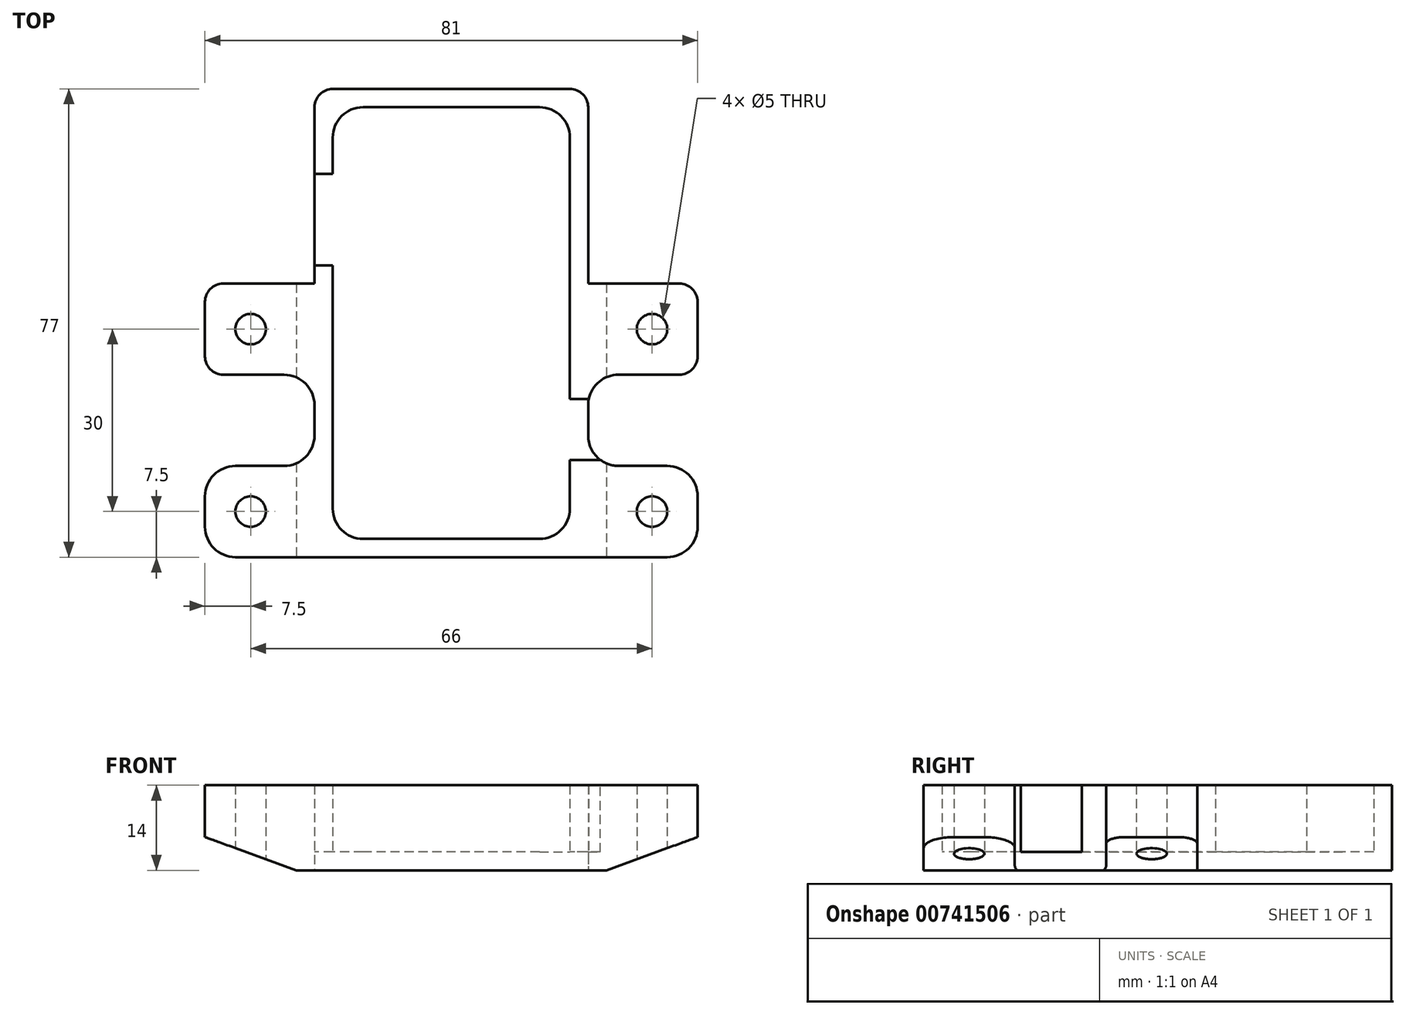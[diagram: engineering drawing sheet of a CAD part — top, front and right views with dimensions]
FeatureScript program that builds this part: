
annotation { "Feature Type Name" : "Feature", "Feature Type Description" : "" }
export const myFeature = defineFeature(function(context is Context, id is Id, definition is map)
    precondition{}
    {
        {
            var Q0;
            Q0=qCreatedBy(makeId("Top.planeOp"),FACE);
            var sketch = newSketch(context, id + "F0", { "sketchPlane" : qUnion([Q0])});
            skLineSegment(sketch, "E0.bottom", {"start": v(22.5, 38.5) * mm, "end": v(-22.5, 38.5) * mm});
            skLineSegment(sketch, "E0.top", {"start": v(22.5, -38.5) * mm, "end": v(-22.5, -38.5) * mm});
            skLineSegment(sketch, "E0.left", {"start": v(22.5, 38.5) * mm, "end": v(22.5, -38.5) * mm});
            skLineSegment(sketch, "E0.right", {"start": v(-22.5, 38.5) * mm, "end": v(-22.5, -38.5) * mm});
            skPoint(sketch, "E0.middle", {"position": v(0, 0) * mm});
            skSolve(sketch);
        }
        {
            var Q0;
            Q0 = qSketchRegion(id + "F0", true);
            extrude(context, id + "F1", {"entities" : qUnion([Q0]), "depth" : 3 * mm, "offsetDistance" : 25 * mm});
        }
        {
            var Q0;
            Q0=makeQuery(id+"F1.opExtrude","CAP_FACE",FACE,{"disambiguationData":[OSD([sQuery(id+"F0.wireOp",EDGE,"E0.bottom"),sQuery(id+"F0.wireOp",EDGE,"E0.top"),sQuery(id+"F0.wireOp",EDGE,"E0.left"),sQuery(id+"F0.wireOp",EDGE,"E0.right")])],"isStart":false});
            var sketch = newSketch(context, id + "F2", { "sketchPlane" : qUnion([Q0])});
            skSolve(sketch);
        }
        {
            var Q0;
            Q0=makeQuery(id+"F2.imprint","IMPRINT",FACE,{"disambiguationData":[TD([[makeQuery(id+"F2.imprint","IMPRINT",EDGE,{"derivedFrom":makeQuery(id+"F1.opExtrude","CAP_EDGE",EDGE,{"disambiguationData":[OSD([sQuery(id+"F0.wireOp",EDGE,"E0.bottom")])],"isStart":false})}),1.0]])]});
            var sketch = newSketch(context, id + "F3", { "sketchPlane" : qUnion([Q0])});
            skLineSegment(sketch, "E1", {"start": v(25.25, -12.5) * mm, "end": v(19.5, -12.5) * mm});
            skLineSegment(sketch, "E2", {"start": v(19.5, -12.5) * mm, "end": v(19.5, 35.5) * mm});
            skLineSegment(sketch, "E3", {"start": v(19.5, 35.5) * mm, "end": v(-19.5, 35.5) * mm});
            skLineSegment(sketch, "E4", {"start": v(-19.5, 35.5) * mm, "end": v(-19.5, 24.5) * mm});
            skLineSegment(sketch, "E5", {"start": v(-19.5, 24.5) * mm, "end": v(-28, 24.5) * mm});
            skLineSegment(sketch, "E6", {"start": v(28, -22.5) * mm, "end": v(19.5, -22.5) * mm});
            skLineSegment(sketch, "E7", {"start": v(19.5, -22.5) * mm, "end": v(19.5, -22.75) * mm});
            skLineSegment(sketch, "E8", {"start": v(19.5, -22.75) * mm, "end": v(19.5, -35.5) * mm});
            skLineSegment(sketch, "E9", {"start": v(-28, 9.5) * mm, "end": v(-19.5, 9.5) * mm});
            skLineSegment(sketch, "E10", {"start": v(-19.5, 9.5) * mm, "end": v(-19.5, -35.5) * mm});
            skPoint(sketch, "E11", {"position": v(-26.46, -18.57) * mm});
            skPoint(sketch, "E12", {"position": v(23.75, -11.55) * mm});
            skPoint(sketch, "E12.positionSnap0", {"position": v(23.75, -22.5) * mm});
            skLineSegment(sketch, "E13", {"start": v(-19.5, -35.5) * mm, "end": v(19.5, -35.5) * mm});
            skSolve(sketch);
        }
        {
            var Q0;
            Q0=makeQuery(id+"F3.imprint","IMPRINT",FACE,{"disambiguationData":[TD([[makeQuery(id+"F3.imprint","IMPRINT",EDGE,{"derivedFrom":sQuery(id+"F3.wireOp",EDGE,"SLzFKG8K-n8H2-2ykC-QiUt-zYdIRSfNmcF6.bottom")}),-1.0]])]});
            var Q1;
            {var subQ2=sQuery(id+"F3.wireOp",EDGE,"E1");Q1=makeQuery(id+"F3.imprint","IMPRINT",FACE,{"disambiguationData":[TD([[makeQuery(id+"F3.imprint","IMPRINT",EDGE,{"derivedFrom":subQ2}),-1.0]])]});}
            var Q2;
            {var subQ3=sQuery(id+"F3.wireOp",EDGE,"E6");Q2=makeQuery(id+"F3.imprint","IMPRINT",FACE,{"disambiguationData":[TD([[makeQuery(id+"F3.imprint","IMPRINT",EDGE,{"derivedFrom":subQ3}),1.0]])]});}
            extrude(context, id + "F4", {"entities" : qUnion([Q0, Q1, Q2]), "operationType" : NewBodyOperationType.ADD, "depth" : 11 * mm, "offsetDistance" : 25 * mm});
        }
        {
            var Q0;
            Q0=qCreatedBy(makeId("Top.planeOp"),FACE);
            var sketch = newSketch(context, id + "F5", { "sketchPlane" : qUnion([Q0])});
            skLineSegment(sketch, "E14.bottom", {"start": v(-22.5, 6.5) * mm, "end": v(-40.5, 6.5) * mm});
            skLineSegment(sketch, "E14.top", {"start": v(-22.5, -8.5) * mm, "end": v(-40.5, -8.5) * mm});
            skLineSegment(sketch, "E14.left", {"start": v(-22.5, 6.5) * mm, "end": v(-22.5, -8.5) * mm});
            skLineSegment(sketch, "E14.right", {"start": v(-40.5, 6.5) * mm, "end": v(-40.5, -8.5) * mm});
            skLineSegment(sketch, "E15.bottom", {"start": v(22.5, 6.5) * mm, "end": v(40.5, 6.5) * mm});
            skLineSegment(sketch, "E15.top", {"start": v(22.5, -8.5) * mm, "end": v(40.5, -8.5) * mm});
            skLineSegment(sketch, "E15.left", {"start": v(22.5, 6.5) * mm, "end": v(22.5, -8.5) * mm});
            skLineSegment(sketch, "E15.right", {"start": v(40.5, 6.5) * mm, "end": v(40.5, -8.5) * mm});
            skCircle(sketch, "E16", {"center": v(33, -1) * mm, "radius": 2.5 * mm});
            skCircle(sketch, "E17", {"center": v(-33, -1) * mm, "radius": 2.5 * mm});
            skPoint(sketch, "E17.centerSnap0", {"position": v(-22.5, -1) * mm});
            skLineSegment(sketch, "E18.bottom", {"start": v(22.5, -23.5) * mm, "end": v(40.5, -23.5) * mm});
            skLineSegment(sketch, "E18.top", {"start": v(22.5, -38.5) * mm, "end": v(40.5, -38.5) * mm});
            skLineSegment(sketch, "E18.left", {"start": v(22.5, -23.5) * mm, "end": v(22.5, -38.5) * mm});
            skLineSegment(sketch, "E18.right", {"start": v(40.5, -23.5) * mm, "end": v(40.5, -38.5) * mm});
            skLineSegment(sketch, "E19.bottom", {"start": v(-22.5, -23.5) * mm, "end": v(-40.5, -23.5) * mm});
            skLineSegment(sketch, "E19.top", {"start": v(-22.5, -38.5) * mm, "end": v(-40.5, -38.5) * mm});
            skLineSegment(sketch, "E19.left", {"start": v(-22.5, -23.5) * mm, "end": v(-22.5, -38.5) * mm});
            skLineSegment(sketch, "E19.right", {"start": v(-40.5, -23.5) * mm, "end": v(-40.5, -38.5) * mm});
            skCircle(sketch, "E20", {"center": v(-33, -31) * mm, "radius": 2.5 * mm});
            skCircle(sketch, "E21", {"center": v(33, -31) * mm, "radius": 2.5 * mm});
            skSolve(sketch);
        }
        {
            var Q0;
            Q0=makeQuery(id+"F5.imprint","IMPRINT",FACE,{"disambiguationData":[TD([[makeQuery(id+"F5.imprint","IMPRINT",EDGE,{"derivedFrom":sQuery(id+"F5.wireOp",EDGE,"E15.bottom")}),-1.0]])]});
            var Q1;
            Q1=makeQuery(id+"F5.imprint","IMPRINT",FACE,{"disambiguationData":[TD([[makeQuery(id+"F5.imprint","IMPRINT",EDGE,{"derivedFrom":sQuery(id+"F5.wireOp",EDGE,"E19.bottom")}),1.0]])]});
            var Q2;
            Q2=makeQuery(id+"F5.imprint","IMPRINT",FACE,{"disambiguationData":[TD([[makeQuery(id+"F5.imprint","IMPRINT",EDGE,{"derivedFrom":sQuery(id+"F5.wireOp",EDGE,"E14.bottom")}),1.0]])]});
            var Q3;
            Q3=makeQuery(id+"F5.imprint","IMPRINT",FACE,{"disambiguationData":[TD([[makeQuery(id+"F5.imprint","IMPRINT",EDGE,{"derivedFrom":sQuery(id+"F5.wireOp",EDGE,"E18.bottom")}),-1.0]])]});
            var Q4;
            Q4=makeQuery(id+"F4.opExtrude","CAP_FACE",FACE,{"disambiguationData":[OSD([sQuery(id+"F0.wireOp",EDGE,"E0.bottom"),sQuery(id+"F0.wireOp",EDGE,"E0.left"),sQuery(id+"F0.wireOp",EDGE,"E0.right"),sQuery(id+"F3.wireOp",EDGE,"E1"),sQuery(id+"F3.wireOp",EDGE,"E2"),sQuery(id+"F3.wireOp",EDGE,"E3"),sQuery(id+"F3.wireOp",EDGE,"E4"),sQuery(id+"F3.wireOp",EDGE,"E5")])],"isStart":false});
            extrude(context, id + "F6", {"entities" : qUnion([Q0, Q1, Q2, Q3]), "operationType" : NewBodyOperationType.ADD, "endBound" : BoundingType.UP_TO_SURFACE, "depth" : 25 * mm, "endBoundEntityFace" : qUnion([Q4]), "offsetDistance" : 25 * mm});
        }
        {
            var Q0;
            {var subQ0=sQuery(id+"F0.wireOp",EDGE,"E0.right");var subQ1=sQuery(id+"F0.wireOp",EDGE,"E0.bottom");Q0=makeQuery(id+"F4.boolean.opBoolean","MERGE",EDGE,{"derivedFrom":[makeQuery(id+"F1.opExtrude","SWEPT_EDGE",EDGE,{"disambiguationData":[OSD([subQ1,subQ0])]}),makeQuery(id+"F4.opExtrude","SWEPT_EDGE",EDGE,{"disambiguationData":[OSD([subQ1,subQ0])]})]});}
            var Q1;
            {var subQ0=sQuery(id+"F0.wireOp",EDGE,"E0.left");var subQ1=sQuery(id+"F0.wireOp",EDGE,"E0.bottom");Q1=makeQuery(id+"F4.boolean.opBoolean","MERGE",EDGE,{"derivedFrom":[makeQuery(id+"F1.opExtrude","SWEPT_EDGE",EDGE,{"disambiguationData":[OSD([subQ1,subQ0])]}),makeQuery(id+"F4.opExtrude","SWEPT_EDGE",EDGE,{"disambiguationData":[OSD([subQ1,subQ0])]})]});}
            var Q2;
            {var subQ0=sQuery(id+"F0.wireOp",EDGE,"E0.right");var subQ1=sQuery(id+"F0.wireOp",EDGE,"E0.top");Q2=makeQuery(id+"F4.boolean.opBoolean","MERGE",EDGE,{"derivedFrom":[makeQuery(id+"F1.opExtrude","SWEPT_EDGE",EDGE,{"disambiguationData":[OSD([subQ1,subQ0])]}),makeQuery(id+"F4.opExtrude","SWEPT_EDGE",EDGE,{"disambiguationData":[OSD([subQ1,subQ0])]})]});}
            var Q3;
            {var subQ0=sQuery(id+"F0.wireOp",EDGE,"E0.left");var subQ1=sQuery(id+"F0.wireOp",EDGE,"E0.top");Q3=makeQuery(id+"F4.boolean.opBoolean","MERGE",EDGE,{"derivedFrom":[makeQuery(id+"F1.opExtrude","SWEPT_EDGE",EDGE,{"disambiguationData":[OSD([subQ1,subQ0])]}),makeQuery(id+"F4.opExtrude","SWEPT_EDGE",EDGE,{"disambiguationData":[OSD([subQ1,subQ0])]})]});}
            var Q4;
            Q4=makeQuery(id+"F6.opExtrude","SWEPT_EDGE",EDGE,{"disambiguationData":[OSD([sQuery(id+"F5.wireOp",EDGE,"E15.bottom"),sQuery(id+"F5.wireOp",EDGE,"E15.right")])]});
            var Q5;
            Q5=makeQuery(id+"F6.opExtrude","SWEPT_EDGE",EDGE,{"disambiguationData":[OSD([sQuery(id+"F5.wireOp",EDGE,"E15.top"),sQuery(id+"F5.wireOp",EDGE,"E15.right")])]});
            var Q6;
            Q6=makeQuery(id+"F6.opExtrude","SWEPT_EDGE",EDGE,{"disambiguationData":[OSD([sQuery(id+"F5.wireOp",EDGE,"E14.bottom"),sQuery(id+"F5.wireOp",EDGE,"E14.right")])]});
            var Q7;
            Q7=makeQuery(id+"F6.opExtrude","SWEPT_EDGE",EDGE,{"disambiguationData":[OSD([sQuery(id+"F5.wireOp",EDGE,"E14.top"),sQuery(id+"F5.wireOp",EDGE,"E14.right")])]});
            fillet(context, id + "F7", {"entities" : qUnion([Q0, Q1, Q2, Q3, Q4, Q5, Q6, Q7]), "radius" : 3 * mm, "tangentPropagation" : true, "allowEdgeOverflow" : false});
        }
        {
            var Q0;
            Q0=makeQuery(id+"F4.opExtrude","SWEPT_EDGE",EDGE,{"disambiguationData":[OSD([sQuery(id+"F3.wireOp",EDGE,"E8"),sQuery(id+"F3.wireOp",EDGE,"E13")])]});
            var Q1;
            Q1=makeQuery(id+"F4.opExtrude","SWEPT_EDGE",EDGE,{"disambiguationData":[OSD([sQuery(id+"F3.wireOp",EDGE,"E10"),sQuery(id+"F3.wireOp",EDGE,"E13")])]});
            var Q2;
            Q2=makeQuery(id+"F4.opExtrude","SWEPT_EDGE",EDGE,{"disambiguationData":[OSD([sQuery(id+"F3.wireOp",EDGE,"E2"),sQuery(id+"F3.wireOp",EDGE,"E3")])]});
            var Q3;
            Q3=makeQuery(id+"F4.opExtrude","SWEPT_EDGE",EDGE,{"disambiguationData":[OSD([sQuery(id+"F3.wireOp",EDGE,"E3"),sQuery(id+"F3.wireOp",EDGE,"E4")])]});
            var Q4;
            Q4=makeQuery(id+"F6.opExtrude","SWEPT_EDGE",EDGE,{"disambiguationData":[OSD([sQuery(id+"F0.wireOp",EDGE,"E0.left"),sQuery(id+"F5.wireOp",EDGE,"E15.bottom"),sQuery(id+"F5.wireOp",EDGE,"E15.left")])]});
            var Q5;
            Q5=makeQuery(id+"F6.opExtrude","SWEPT_EDGE",EDGE,{"disambiguationData":[OSD([sQuery(id+"F0.wireOp",EDGE,"E0.left"),sQuery(id+"F5.wireOp",EDGE,"E15.top"),sQuery(id+"F5.wireOp",EDGE,"E15.left")])]});
            var Q6;
            Q6=makeQuery(id+"F6.opExtrude","SWEPT_EDGE",EDGE,{"disambiguationData":[OSD([sQuery(id+"F0.wireOp",EDGE,"E0.right"),sQuery(id+"F5.wireOp",EDGE,"E14.top"),sQuery(id+"F5.wireOp",EDGE,"E14.left")])]});
            var Q7;
            Q7=makeQuery(id+"F6.opExtrude","SWEPT_EDGE",EDGE,{"disambiguationData":[OSD([sQuery(id+"F0.wireOp",EDGE,"E0.right"),sQuery(id+"F5.wireOp",EDGE,"E14.bottom"),sQuery(id+"F5.wireOp",EDGE,"E14.left")])]});
            fillet(context, id + "F8", {"entities" : qUnion([Q0, Q1, Q2, Q3, Q4, Q5, Q6, Q7]), "radius" : 5 * mm, "tangentPropagation" : true, "allowEdgeOverflow" : false});
        }
        {
            var Q0;
            Q0=makeQuery(id+"F6.opExtrude","SWEPT_EDGE",EDGE,{"disambiguationData":[OSD([sQuery(id+"F5.wireOp",EDGE,"E19.bottom"),sQuery(id+"F5.wireOp",EDGE,"E19.right")])]});
            var Q1;
            Q1=makeQuery(id+"F6.opExtrude","SWEPT_EDGE",EDGE,{"disambiguationData":[OSD([sQuery(id+"F5.wireOp",EDGE,"E19.bottom"),sQuery(id+"F5.wireOp",EDGE,"E19.left")])]});
            var Q2;
            Q2=makeQuery(id+"F6.opExtrude","SWEPT_EDGE",EDGE,{"disambiguationData":[OSD([sQuery(id+"F5.wireOp",EDGE,"E19.top"),sQuery(id+"F5.wireOp",EDGE,"E19.right")])]});
            var Q3;
            Q3=makeQuery(id+"F6.opExtrude","SWEPT_EDGE",EDGE,{"disambiguationData":[OSD([sQuery(id+"F5.wireOp",EDGE,"E18.top"),sQuery(id+"F5.wireOp",EDGE,"E18.right")])]});
            var Q4;
            Q4=makeQuery(id+"F6.opExtrude","SWEPT_EDGE",EDGE,{"disambiguationData":[OSD([sQuery(id+"F5.wireOp",EDGE,"E18.bottom"),sQuery(id+"F5.wireOp",EDGE,"E18.right")])]});
            var Q5;
            Q5=makeQuery(id+"F6.opExtrude","SWEPT_EDGE",EDGE,{"disambiguationData":[OSD([sQuery(id+"F5.wireOp",EDGE,"E18.bottom"),sQuery(id+"F5.wireOp",EDGE,"E18.left")])]});
            fillet(context, id + "F9", {"entities" : qUnion([Q0, Q1, Q2, Q3, Q4, Q5]), "radius" : 5 * mm, "tangentPropagation" : true, "allowEdgeOverflow" : false});
        }
        {
            var Q0;
            {var subQ0=sQuery(id+"F0.wireOp",EDGE,"E0.top");Q0=makeQuery(id+"F6.boolean.opBoolean","MERGE",FACE,{"derivedFrom":[makeQuery(id+"F4.boolean.opBoolean","MERGE",FACE,{"derivedFrom":[makeQuery(id+"F1.opExtrude","SWEPT_FACE",FACE,{"disambiguationData":[OSD([subQ0])]}),makeQuery(id+"F4.opExtrude","SWEPT_FACE",FACE,{"disambiguationData":[OSD([subQ0])]})]}),makeQuery(id+"F6.opExtrude","SWEPT_FACE",FACE,{"disambiguationData":[OSD([sQuery(id+"F5.wireOp",EDGE,"E18.top")])]}),makeQuery(id+"F6.opExtrude","SWEPT_FACE",FACE,{"disambiguationData":[OSD([sQuery(id+"F5.wireOp",EDGE,"E19.top")])]})]});}
            var sketch = newSketch(context, id + "F10", { "sketchPlane" : qUnion([Q0])});
            skLineSegment(sketch, "E22", {"start": v(25.5, 0) * mm, "end": v(46.65, 7.7) * mm});
            skLineSegment(sketch, "E23", {"start": v(-25.5, 0) * mm, "end": v(-49.43, 8.7) * mm});
            skLineSegment(sketch, "E24", {"start": v(-49.43, 8.7) * mm, "end": v(-49.43, 0) * mm});
            skLineSegment(sketch, "E25", {"start": v(-49.43, 0) * mm, "end": v(-25.5, 0) * mm});
            skLineSegment(sketch, "E26", {"start": v(46.65, 7.7) * mm, "end": v(46.65, 0) * mm});
            skLineSegment(sketch, "E27", {"start": v(46.65, 0) * mm, "end": v(25.5, 0) * mm});
            skSolve(sketch);
        }
        {
            var Q0;
            {var subQ0=sQuery(id+"F10.wireOp",EDGE,"E25");var subQ1=sQuery(id+"F10.wireOp",EDGE,"E23");var subQ2=sQuery(id+"F5.wireOp",EDGE,"E19.top");var subQ3=sQuery(id+"F5.wireOp",EDGE,"E18.top");var subQ4=sQuery(id+"F0.wireOp",EDGE,"E0.top");var subQ5=makeQuery(id+"F10.imprint","INTERSECT",VERTEX,{"derivedFrom":[makeQuery(id+"F6.boolean.opBoolean","MERGE",EDGE,{"derivedFrom":[makeQuery(id+"F1.opExtrude","CAP_EDGE",EDGE,{"disambiguationData":[OSD([subQ4])],"isStart":true}),makeQuery(id+"F6.opExtrude","CAP_EDGE",EDGE,{"disambiguationData":[OSD([subQ3])],"isStart":true}),makeQuery(id+"F6.opExtrude","CAP_EDGE",EDGE,{"disambiguationData":[OSD([subQ2])],"isStart":true})]}),subQ1,subQ0]});Q0=makeQuery(id+"F10.imprint","IMPRINT",FACE,{"disambiguationData":[TD([[makeQuery(id+"F10.imprint","IMPRINT",EDGE,{"disambiguationData":[TD([[subQ5,-1.0]])],"derivedFrom":subQ1}),1.0]])]});}
            var Q1;
            {var subQ0=sQuery(id+"F10.wireOp",EDGE,"E24");Q1=makeQuery(id+"F10.imprint","IMPRINT",FACE,{"disambiguationData":[TD([[makeQuery(id+"F10.imprint","IMPRINT",EDGE,{"derivedFrom":subQ0}),1.0]])]});}
            var Q2;
            {var subQ0=sQuery(id+"F10.wireOp",EDGE,"E27");var subQ1=sQuery(id+"F10.wireOp",EDGE,"E22");var subQ2=sQuery(id+"F5.wireOp",EDGE,"E19.top");var subQ3=sQuery(id+"F5.wireOp",EDGE,"E18.top");var subQ4=sQuery(id+"F0.wireOp",EDGE,"E0.top");var subQ5=makeQuery(id+"F10.imprint","INTERSECT",VERTEX,{"derivedFrom":[makeQuery(id+"F6.boolean.opBoolean","MERGE",EDGE,{"derivedFrom":[makeQuery(id+"F1.opExtrude","CAP_EDGE",EDGE,{"disambiguationData":[OSD([subQ4])],"isStart":true}),makeQuery(id+"F6.opExtrude","CAP_EDGE",EDGE,{"disambiguationData":[OSD([subQ3])],"isStart":true}),makeQuery(id+"F6.opExtrude","CAP_EDGE",EDGE,{"disambiguationData":[OSD([subQ2])],"isStart":true})]}),subQ1,subQ0]});Q2=makeQuery(id+"F10.imprint","IMPRINT",FACE,{"disambiguationData":[TD([[makeQuery(id+"F10.imprint","IMPRINT",EDGE,{"disambiguationData":[TD([[subQ5,-1.0]])],"derivedFrom":subQ1}),-1.0]])]});}
            var Q3;
            {var subQ0=sQuery(id+"F10.wireOp",EDGE,"E26");Q3=makeQuery(id+"F10.imprint","IMPRINT",FACE,{"disambiguationData":[TD([[makeQuery(id+"F10.imprint","IMPRINT",EDGE,{"derivedFrom":subQ0}),-1.0]])]});}
            extrude(context, id + "F11", {"entities" : qUnion([Q0, Q1, Q2, Q3]), "operationType" : NewBodyOperationType.REMOVE, "endBound" : BoundingType.THROUGH_ALL, "oppositeDirection" : true, "depth" : 25 * mm, "offsetDistance" : 25 * mm});
        }
    });
